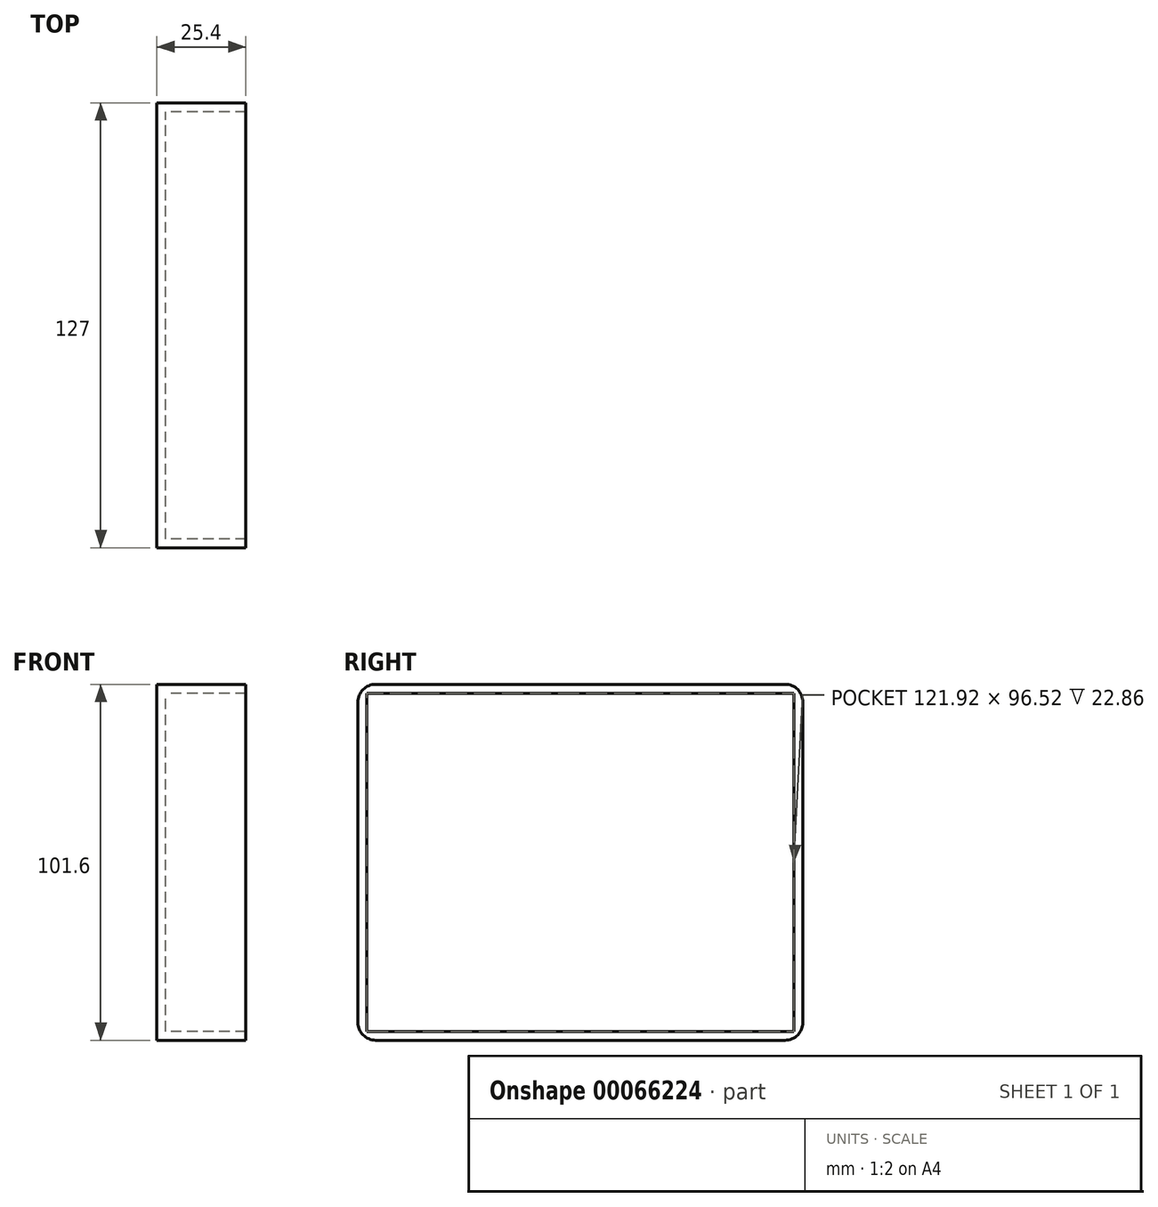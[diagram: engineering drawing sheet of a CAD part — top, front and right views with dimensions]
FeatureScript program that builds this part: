
annotation { "Feature Type Name" : "Feature", "Feature Type Description" : "" }
export const myFeature = defineFeature(function(context is Context, id is Id, definition is map)
    precondition{}
    {
        {
            var Q0;
            Q0=qCreatedBy(makeId("Right.planeOp"),FACE);
            var sketch = newSketch(context, id + "F0", { "sketchPlane" : qUnion([Q0])});
            skLineSegment(sketch, "E0.bottom", {"start": v(0, 0) * mm, "end": v(127, 0) * mm});
            skLineSegment(sketch, "E0.top", {"start": v(0, 101.6) * mm, "end": v(127, 101.6) * mm});
            skLineSegment(sketch, "E0.left", {"start": v(0, 0) * mm, "end": v(0, 101.6) * mm});
            skLineSegment(sketch, "E0.right", {"start": v(127, 0) * mm, "end": v(127, 101.6) * mm});
            skSolve(sketch);
        }
        {
            var Q0;
            Q0 = qSketchRegion(id + "F0", true);
            extrude(context, id + "F1", {"entities" : qUnion([Q0]), "depth" : 25.4 * mm});
        }
        {
            var Q0;
            Q0 = qSketchRegion(id + "F0", true);
            extrude(context, id + "F2", {"entities" : qUnion([Q0]), "operationType" : NewBodyOperationType.ADD, "depth" : 6.35 * mm});
        }
        {
            var Q0;
            Q0=makeQuery(id+"F1.opExtrude","CAP_FACE",FACE,{"disambiguationData":[OSD([sQuery(id+"F0.wireOp",EDGE,"E0.bottom"),sQuery(id+"F0.wireOp",EDGE,"E0.top"),sQuery(id+"F0.wireOp",EDGE,"E0.left"),sQuery(id+"F0.wireOp",EDGE,"E0.right")])],"isStart":false});
            shell(context, id + "F3", {"entities" : qUnion([Q0]), "thickness" : 2.54 * mm});
        }
        {
            var Q0;
            Q0=makeQuery(id+"F1.opExtrude","SWEPT_EDGE",EDGE,{"disambiguationData":[OSD([sQuery(id+"F0.wireOp",EDGE,"E0.top"),sQuery(id+"F0.wireOp",EDGE,"E0.left")])]});
            var Q1;
            Q1=makeQuery(id+"F1.opExtrude","SWEPT_EDGE",EDGE,{"disambiguationData":[OSD([sQuery(id+"F0.wireOp",EDGE,"E0.bottom"),sQuery(id+"F0.wireOp",EDGE,"E0.left")])]});
            var Q2;
            Q2=makeQuery(id+"F1.opExtrude","SWEPT_EDGE",EDGE,{"disambiguationData":[OSD([sQuery(id+"F0.wireOp",EDGE,"E0.bottom"),sQuery(id+"F0.wireOp",EDGE,"E0.right")])]});
            var Q3;
            Q3=makeQuery(id+"F1.opExtrude","SWEPT_EDGE",EDGE,{"disambiguationData":[OSD([sQuery(id+"F0.wireOp",EDGE,"E0.top"),sQuery(id+"F0.wireOp",EDGE,"E0.right")])]});
            fillet(context, id + "F4", {"entities" : qUnion([Q0, Q1, Q2, Q3]), "radius" : 5.08 * mm, "tangentPropagation" : true, "allowEdgeOverflow" : false});
        }
    });
